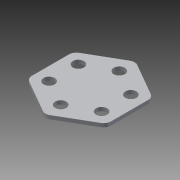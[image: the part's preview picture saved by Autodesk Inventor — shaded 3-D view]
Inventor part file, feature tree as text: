
AUTODESK INVENTOR PART (.ipt)
format: ipt  version: 2014 (Build 180170000, 170)  size: 126,464 bytes
history: native  units: in
note: dims shown in document units (in); Inventor stores cm internally (conversion verified against a paired STEP export)
features: extrude x1, sketch x1
ambient origin geometry x8: Origin, YZ Plane, XZ Plane, XY Plane, X Axis, Y Axis, Z Axis, Center Point
bodies: Solid1 (feature_tree)
feature tree (2):
  extrude  "Extrusion1"  Depth=1.0in
  sketch  "Sketch1"  dims[d1=0.19in d2=1.0in d3=0.19in d4=0.19in d5=0.5in d6=0.4485in d7=0.4485in d8=0.25in d9=0.19in d10=0.19in d11=0.4485in d12=0.5in d13=1.35in d14=0.125in d15=0.0625in d16=0.0in]
